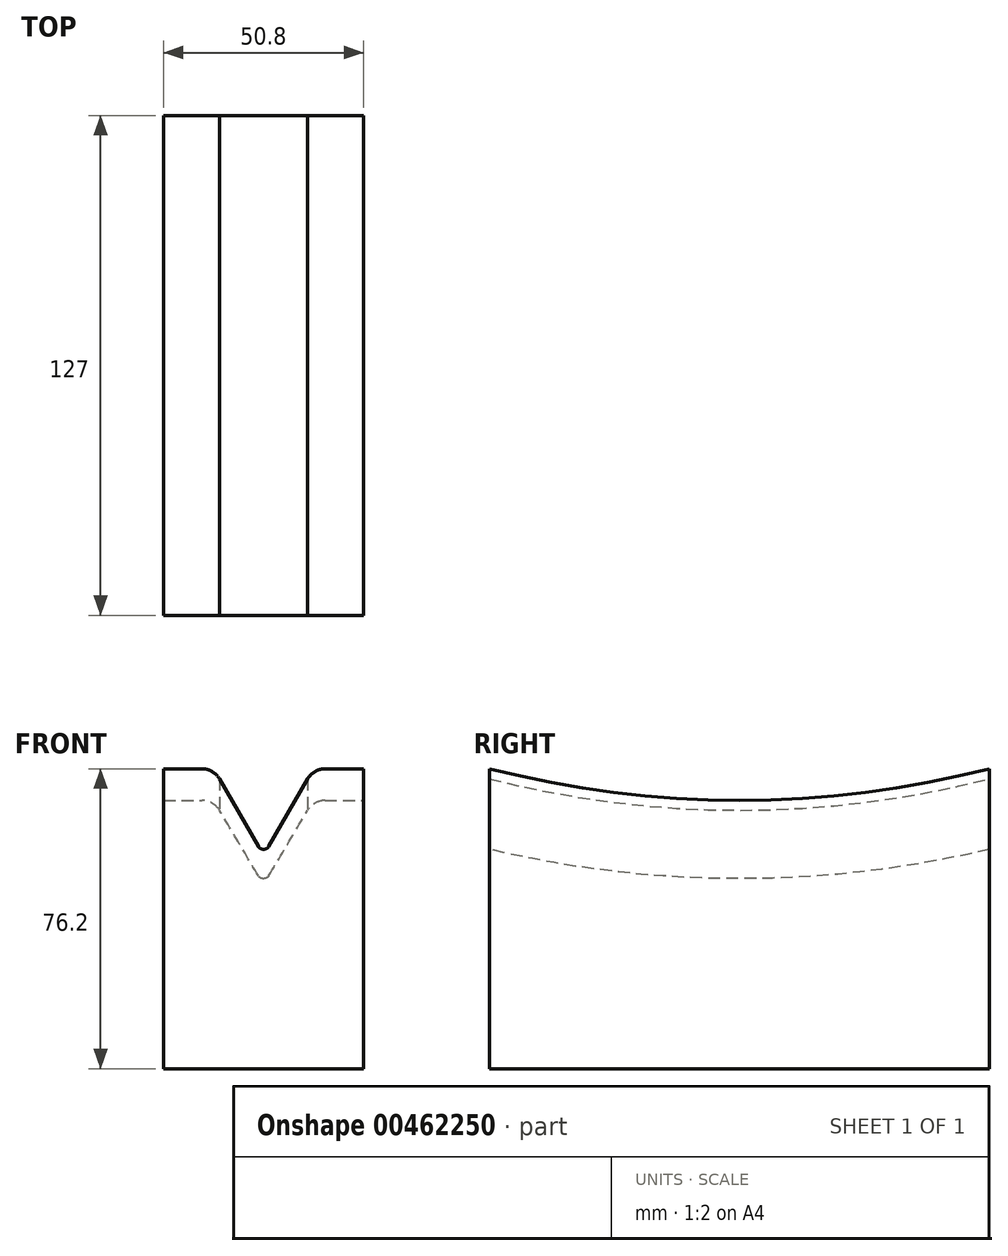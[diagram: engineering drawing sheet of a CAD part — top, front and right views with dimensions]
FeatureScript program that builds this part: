
annotation { "Feature Type Name" : "Feature", "Feature Type Description" : "" }
export const myFeature = defineFeature(function(context is Context, id is Id, definition is map)
    precondition{}
    {
        {
            var Q0;
            Q0=qCreatedBy(makeId("Front.planeOp"),FACE);
            var sketch = newSketch(context, id + "F0", { "sketchPlane" : qUnion([Q0])});
            skLineSegment(sketch, "E0.bottom", {"start": v(-25.4, 0) * mm, "end": v(25.4, 0) * mm});
            skLineSegment(sketch, "E0.top", {"start": v(-25.4, -76.2) * mm, "end": v(25.4, -76.2) * mm});
            skLineSegment(sketch, "E0.left", {"start": v(-25.4, 0) * mm, "end": v(-25.4, -76.2) * mm});
            skLineSegment(sketch, "E0.right", {"start": v(25.4, 0) * mm, "end": v(25.4, -76.2) * mm});
            skSolve(sketch);
        }
        {
            var Q0;
            Q0 = qSketchRegion(id + "F0", true);
            extrude(context, id + "F1", {"entities" : qUnion([Q0]), "oppositeDirection" : true, "depth" : 127 * mm, "offsetDistance" : 25.4 * mm});
        }
        {
            var Q0;
            Q0=qCreatedBy(makeId("Right.planeOp"),FACE);
            var sketch = newSketch(context, id + "F2", { "sketchPlane" : qUnion([Q0])});
            skCircle(sketch, "E1", {"center": v(63.5, 245.93) * mm, "radius": 254 * mm});
            skSolve(sketch);
        }
        {
            var Q0;
            Q0=qCreatedBy(makeId("Front.planeOp"),FACE);
            var sketch = newSketch(context, id + "F3", { "sketchPlane" : qUnion([Q0])});
            skLineSegment(sketch, "E2", {"start": v(-12.7, 0) * mm, "end": v(12.7, 0) * mm, "construction": true});
            skLineSegment(sketch, "E3", {"start": v(12.7, 0) * mm, "end": v(1.32, -19.71) * mm});
            skLineSegment(sketch, "E4", {"start": v(-1.32, -19.71) * mm, "end": v(-12.7, 0) * mm});
            skPoint(sketch, "E5.visualSharp", {"position": v(0, -22) * mm});
            skArc(sketch, "E5.filletArc", {"start": v(-1.32, -19.71) * mm, "mid": v(0, -20.47) * mm, "end": v(1.32, -19.71) * mm});
            skLineSegment(sketch, "E6", {"start": v(-12.7, 0) * mm, "end": v(-29.69, 0) * mm});
            skLineSegment(sketch, "E7", {"start": v(-29.69, 0) * mm, "end": v(-29.69, 26.45) * mm});
            skLineSegment(sketch, "E8", {"start": v(-29.69, 26.45) * mm, "end": v(43.41, 26.45) * mm});
            skLineSegment(sketch, "E9", {"start": v(43.41, 26.45) * mm, "end": v(43.41, 0) * mm});
            skLineSegment(sketch, "E10", {"start": v(43.41, 0) * mm, "end": v(12.7, 0) * mm});
            skSolve(sketch);
        }
        {
            var Q0;
            Q0=makeQuery(id+"F3.imprint","IMPRINT",FACE,{"disambiguationData":[TD([[makeQuery(id+"F3.imprint","IMPRINT",EDGE,{"derivedFrom":sQuery(id+"F3.wireOp",EDGE,"E3")}),-1.0]])]});
            var Q1;
            Q1=sQuery(id+"F2.wireOp",EDGE,"E1");
            sweep(context, id + "F4", {"operationType" : NewBodyOperationType.REMOVE, "profiles" : qUnion([Q0]), "path" : qUnion([Q1])});
        }
        {
            var Q0;
            Q0=makeQuery(id+"F4.boolean.opBoolean","COPY",EDGE,{"derivedFrom":makeQuery(id+"F4.opSweep","SWEPT_EDGE",EDGE,{"disambiguationData":[OSD([sQuery(id+"F2.wireOp",EDGE,"E1"),sQuery(id+"F3.wireOp",EDGE,"E4"),sQuery(id+"F3.wireOp",EDGE,"E6")])]})});
            var Q1;
            Q1=makeQuery(id+"F4.boolean.opBoolean","COPY",EDGE,{"derivedFrom":makeQuery(id+"F4.opSweep","SWEPT_EDGE",EDGE,{"disambiguationData":[OSD([sQuery(id+"F2.wireOp",EDGE,"E1"),sQuery(id+"F3.wireOp",EDGE,"E3"),sQuery(id+"F3.wireOp",EDGE,"E10")])]})});
            fillet(context, id + "F5", {"entities" : qUnion([Q0, Q1]), "radius" : 5.08 * mm, "tangentPropagation" : true, "allowEdgeOverflow" : false});
        }
    });
